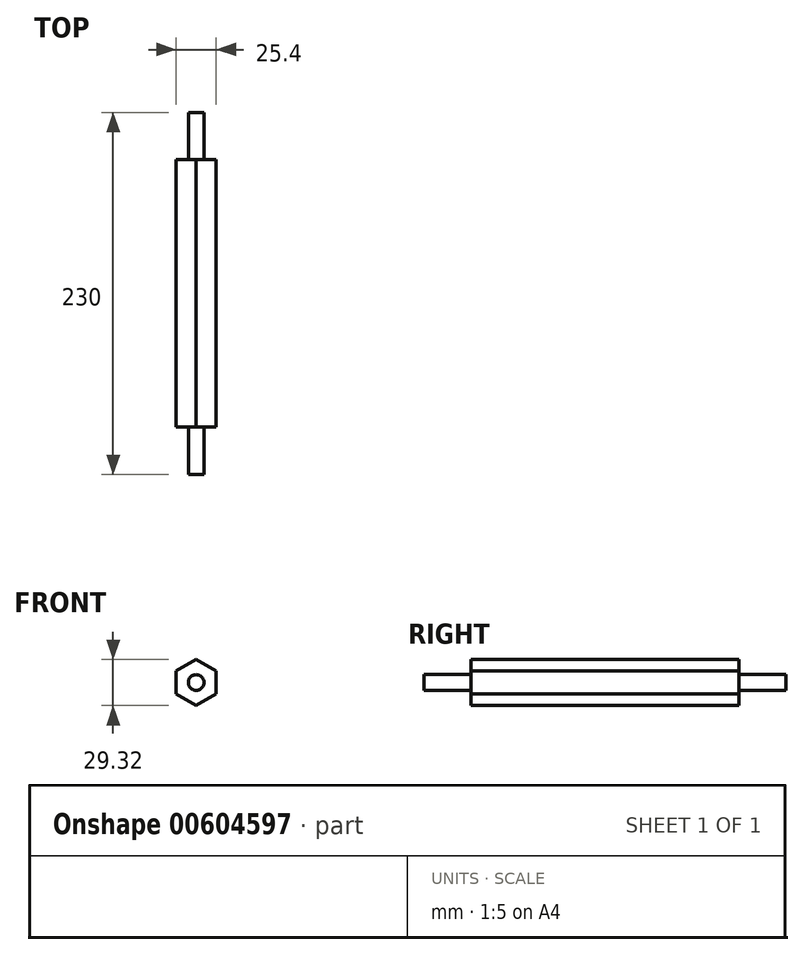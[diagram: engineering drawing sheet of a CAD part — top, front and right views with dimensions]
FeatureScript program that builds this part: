
annotation { "Feature Type Name" : "Feature", "Feature Type Description" : "" }
export const myFeature = defineFeature(function(context is Context, id is Id, definition is map)
    precondition{}
    {
        {
            var Q0;
            Q0=qCreatedBy(makeId("Front.planeOp"),FACE);
            var sketch = newSketch(context, id + "F0", { "sketchPlane" : qUnion([Q0])});
            skLineSegment(sketch, "E0.0", {"start": v(-12.7, -7.33) * mm, "end": v(-12.7, 7.33) * mm});
            skLineSegment(sketch, "E0.1", {"start": v(-12.7, 7.33) * mm, "end": v(0, 14.66) * mm});
            skLineSegment(sketch, "E0.2", {"start": v(0, 14.66) * mm, "end": v(12.7, 7.33) * mm});
            skLineSegment(sketch, "E0.3", {"start": v(12.7, 7.33) * mm, "end": v(12.7, -7.33) * mm});
            skLineSegment(sketch, "E0.4", {"start": v(12.7, -7.33) * mm, "end": v(0, -14.66) * mm});
            skLineSegment(sketch, "E0.5", {"start": v(0, -14.66) * mm, "end": v(-12.7, -7.33) * mm});
            skSolve(sketch);
        }
        {
            var Q0;
            Q0=makeQuery(id+"F0.imprint","IMPRINT",FACE,{"disambiguationData":[TD([[makeQuery(id+"F0.imprint","IMPRINT",EDGE,{"derivedFrom":sQuery(id+"F0.wireOp",EDGE,"26b7bdf0-0a2f-4e52-a962-ef4c22370b04.0")}),-1.0]])]});
            var Q1;
            Q1=makeQuery(id+"F0.imprint","IMPRINT",FACE,{"disambiguationData":[TD([[makeQuery(id+"F0.imprint","IMPRINT",EDGE,{"derivedFrom":sQuery(id+"F0.wireOp",EDGE,"E0.0")}),-1.0]])]});
            extrude(context, id + "F1", {"entities" : qUnion([Q0, Q1]), "depth" : 170 * mm, "offsetDistance" : 25 * mm});
        }
        {
            var Q0;
            Q0=makeQuery(id+"F1.opExtrude","CAP_FACE",FACE,{"disambiguationData":[OSD([sQuery(id+"F0.wireOp",EDGE,"E0.0"),sQuery(id+"F0.wireOp",EDGE,"E0.1"),sQuery(id+"F0.wireOp",EDGE,"E0.2"),sQuery(id+"F0.wireOp",EDGE,"E0.3"),sQuery(id+"F0.wireOp",EDGE,"E0.4"),sQuery(id+"F0.wireOp",EDGE,"E0.5")])],"isStart":true});
            var sketch = newSketch(context, id + "F2", { "sketchPlane" : qUnion([Q0])});
            skCircle(sketch, "E1", {"center": v(0, 0) * mm, "radius": 5 * mm});
            skSolve(sketch);
        }
        {
            var Q0;
            Q0=makeQuery(id+"F2.imprint","IMPRINT",FACE,{"disambiguationData":[TD([[makeQuery(id+"F2.imprint","IMPRINT",EDGE,{"derivedFrom":sQuery(id+"F2.wireOp",EDGE,"E1")}),1.0]])]});
            extrude(context, id + "F3", {"entities" : qUnion([Q0]), "operationType" : NewBodyOperationType.ADD, "depth" : 30 * mm, "offsetDistance" : 25 * mm});
        }
        {
            var Q0;
            Q0=makeQuery(id+"F1.opExtrude","CAP_FACE",FACE,{"disambiguationData":[OSD([sQuery(id+"F0.wireOp",EDGE,"E0.0"),sQuery(id+"F0.wireOp",EDGE,"E0.1"),sQuery(id+"F0.wireOp",EDGE,"E0.2"),sQuery(id+"F0.wireOp",EDGE,"E0.3"),sQuery(id+"F0.wireOp",EDGE,"E0.4"),sQuery(id+"F0.wireOp",EDGE,"E0.5")])],"isStart":false});
            var sketch = newSketch(context, id + "F4", { "sketchPlane" : qUnion([Q0])});
            skCircle(sketch, "E2", {"center": v(0, 0) * mm, "radius": 5 * mm});
            skSolve(sketch);
        }
        {
            var Q0;
            Q0=qSketchRegion(id+"F4",true);
            extrude(context, id + "F5", {"entities" : qUnion([Q0]), "operationType" : NewBodyOperationType.ADD, "depth" : 30 * mm, "offsetDistance" : 25 * mm});
        }
    });
